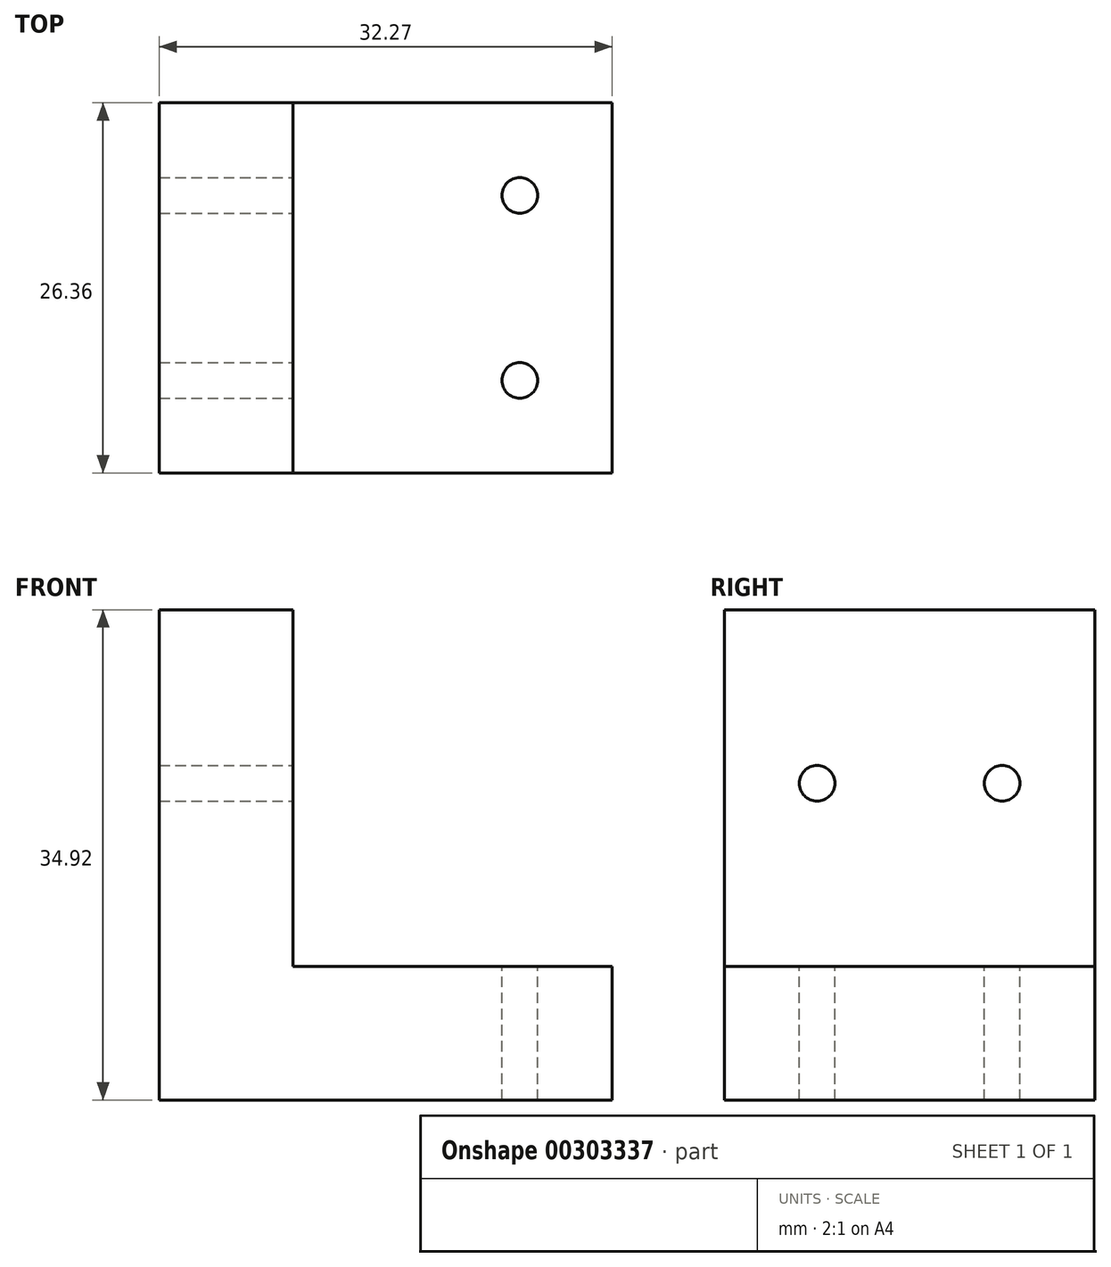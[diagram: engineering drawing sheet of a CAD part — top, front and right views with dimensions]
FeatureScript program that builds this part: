
annotation { "Feature Type Name" : "Feature", "Feature Type Description" : "" }
export const myFeature = defineFeature(function(context is Context, id is Id, definition is map)
    precondition{}
    {
        {
            var Q0;
            Q0=qCreatedBy(makeId("Front.planeOp"),FACE);
            var sketch = newSketch(context, id + "F0", { "sketchPlane" : qUnion([Q0])});
            skLineSegment(sketch, "E0.bottom", {"start": v(-31.57, 17) * mm, "end": v(-22.04, 17) * mm});
            skLineSegment(sketch, "E0.left", {"start": v(-31.57, 17) * mm, "end": v(-31.57, -17.93) * mm});
            skLineSegment(sketch, "E0.right", {"start": v(-22.04, 17) * mm, "end": v(-22.04, -8.4) * mm});
            skLineSegment(sketch, "E1.top", {"start": v(-22.04, -8.4) * mm, "end": v(0.7, -8.4) * mm});
            skLineSegment(sketch, "E1.right", {"start": v(0.7, -17.93) * mm, "end": v(0.7, -8.4) * mm});
            skLineSegment(sketch, "E2", {"start": v(-31.57, -17.93) * mm, "end": v(0.7, -17.93) * mm});
            skSolve(sketch);
        }
        {
            var Q0;
            Q0=makeQuery(id+"F0.imprint","IMPRINT",FACE,{"disambiguationData":[TD([[makeQuery(id+"F0.imprint","IMPRINT",EDGE,{"derivedFrom":sQuery(id+"F0.wireOp",EDGE,"E0.bottom")}),-1.0]])]});
            extrude(context, id + "F1", {"entities" : qUnion([Q0]), "endBound" : BoundingType.SYMMETRIC, "depth" : 26.37 * mm});
        }
        {
            var Q0;
            Q0=makeQuery(id+"F1.opExtrude","SWEPT_FACE",FACE,{"disambiguationData":[OSD([sQuery(id+"F0.wireOp",EDGE,"E1.top")])]});
            var sketch = newSketch(context, id + "F2", { "sketchPlane" : qUnion([Q0])});
            skCircle(sketch, "E3.2.5.0", {"center": v(-5.89, 6.6) * mm, "radius": 2.31 * mm});
            skCircle(sketch, "E3.2.6.0", {"center": v(-5.89, -6.6) * mm, "radius": 2.31 * mm});
            skSolve(sketch);
        }
        {
            var Q0;
            Q0=sQuery(id+"F2.wireOp",VERTEX,"E3.2.5.0.center");
            var Q1;
            Q1=sQuery(id+"F2.wireOp",VERTEX,"E3.2.6.0.center");
            var Q2;
            Q2=makeQuery(id+"F1.opExtrude","SWEPT_BODY",BODY,{"disambiguationData":[OSD([sQuery(id+"F0.wireOp",EDGE,"E0.bottom"),sQuery(id+"F0.wireOp",EDGE,"E0.left"),sQuery(id+"F0.wireOp",EDGE,"E0.right"),sQuery(id+"F0.wireOp",EDGE,"E1.top"),sQuery(id+"F0.wireOp",EDGE,"E1.right"),sQuery(id+"F0.wireOp",EDGE,"E2")])]});
            hole(context, id + "F3", {"style" : HoleStyle.SIMPLE, "endStyle" : HoleEndStyle.THROUGH, "holeDiameter" : 2.54 * mm, "tappedDepth" : 12.7 * mm, "tapClearance" : 3, "locations" : qUnion([Q0, Q1]), "scope" : qUnion([Q2])});
        }
        {
            var Q0;
            Q0=makeQuery(id+"F1.opExtrude","SWEPT_FACE",FACE,{"disambiguationData":[OSD([sQuery(id+"F0.wireOp",EDGE,"E0.right")])]});
            var sketch = newSketch(context, id + "F4", { "sketchPlane" : qUnion([Q0])});
            skCircle(sketch, "E4.2.6.0", {"center": v(-6.6, 4.63) * mm, "radius": 2.31 * mm});
            skCircle(sketch, "E4.3.6.0", {"center": v(6.6, 4.63) * mm, "radius": 2.31 * mm});
            skSolve(sketch);
        }
        {
            var Q0;
            Q0=sQuery(id+"F4.wireOp",VERTEX,"E4.2.6.0.center");
            var Q1;
            Q1=sQuery(id+"F4.wireOp",VERTEX,"E4.3.6.0.center");
            var Q2;
            Q2=makeQuery(id+"F1.opExtrude","SWEPT_BODY",BODY,{"disambiguationData":[OSD([sQuery(id+"F0.wireOp",EDGE,"E0.bottom"),sQuery(id+"F0.wireOp",EDGE,"E0.left"),sQuery(id+"F0.wireOp",EDGE,"E0.right"),sQuery(id+"F0.wireOp",EDGE,"E1.top"),sQuery(id+"F0.wireOp",EDGE,"E1.right"),sQuery(id+"F0.wireOp",EDGE,"E2")])]});
            hole(context, id + "F5", {"style" : HoleStyle.SIMPLE, "endStyle" : HoleEndStyle.THROUGH, "holeDiameter" : 2.54 * mm, "tappedDepth" : 12.7 * mm, "tapClearance" : 3, "locations" : qUnion([Q0, Q1]), "scope" : qUnion([Q2])});
        }
    });
